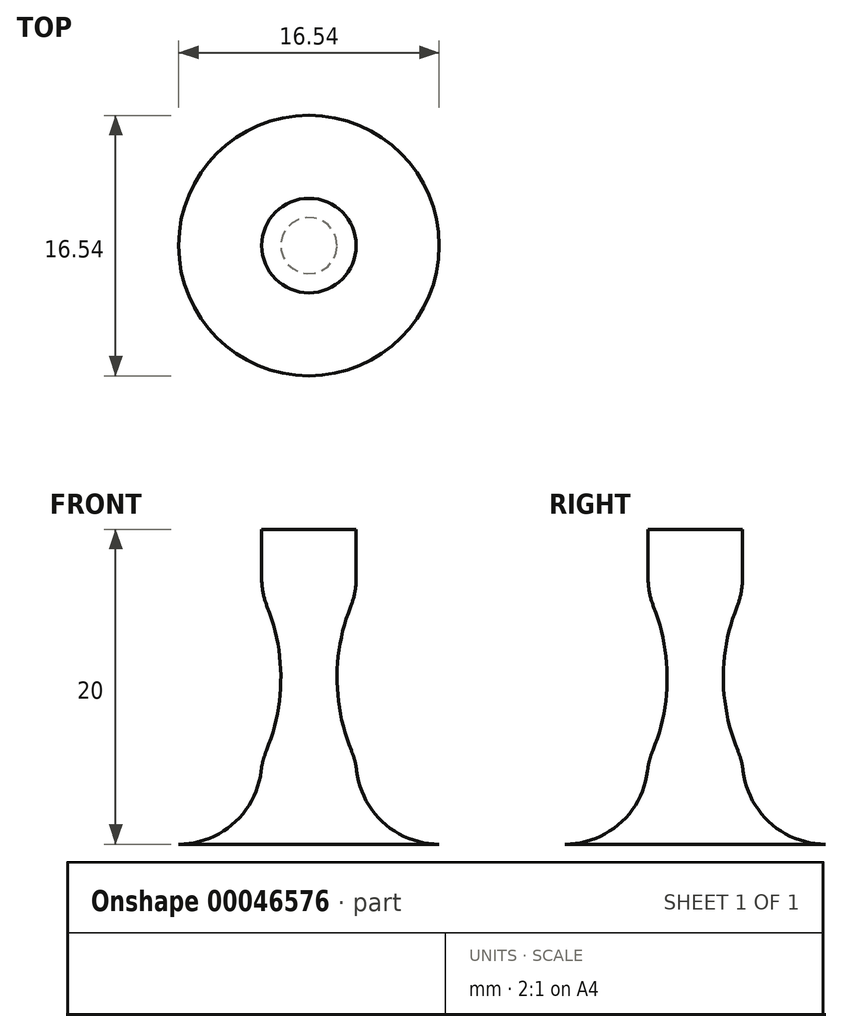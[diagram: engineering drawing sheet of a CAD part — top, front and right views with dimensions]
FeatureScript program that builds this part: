
annotation { "Feature Type Name" : "Feature", "Feature Type Description" : "" }
export const myFeature = defineFeature(function(context is Context, id is Id, definition is map)
    precondition{}
    {
        {
            var Q0;
            Q0=qCreatedBy(makeId("Front.planeOp"),FACE);
            var sketch = newSketch(context, id + "F0", { "sketchPlane" : qUnion([Q0])});
            skLineSegment(sketch, "E0", {"start": v(-3, 0) * mm, "end": v(0, 0) * mm});
            skLineSegment(sketch, "E1", {"start": v(0, 20) * mm, "end": v(0, 0) * mm});
            skLineSegment(sketch, "E2", {"start": v(0, 20) * mm, "end": v(-3, 20) * mm});
            skLineSegment(sketch, "E3", {"start": v(-3, 20) * mm, "end": v(-3, 15.88) * mm});
            skArc(sketch, "E4", {"start": v(-3, 5.27) * mm, "mid": v(-1.78, 10.58) * mm, "end": v(-3, 15.88) * mm});
            skLineSegment(sketch, "E5.trimOffspring", {"start": v(-3, 5.27) * mm, "end": v(-3, 0) * mm});
            skArc(sketch, "E6", {"start": v(-8.27, 0) * mm, "mid": v(-4.54, 1.54) * mm, "end": v(-3, 5.27) * mm});
            skLineSegment(sketch, "E7", {"start": v(-8.27, 0) * mm, "end": v(-3, 0) * mm});
            skSolve(sketch);
        }
        {
            var Q0;
            Q0 = qSketchRegion(id + "F0", true);
            var Q1;
            Q1=sQuery(id+"F0.wireOp",EDGE,"E1");
            revolve(context, id + "F1", {"entities" : qUnion([Q0]), "axis" : qUnion([Q1]), "revolveType" : RevolveType.FULL});
        }
        {
            var Q0;
            Q0=makeQuery(id+"F1.opRevolve","SWEPT_EDGE",EDGE,{"disambiguationData":[OSD([sQuery(id+"F0.wireOp",EDGE,"E3"),sQuery(id+"F0.wireOp",EDGE,"E4")])]});
            var Q1;
            Q1=makeQuery(id+"F1.opRevolve","SWEPT_EDGE",EDGE,{"disambiguationData":[OSD([sQuery(id+"F0.wireOp",EDGE,"E4"),sQuery(id+"F0.wireOp",EDGE,"E5.trimOffspring"),sQuery(id+"F0.wireOp",EDGE,"E6")])]});
            fillet(context, id + "F2", {"entities" : qUnion([Q0, Q1]), "radius" : 5 * mm, "tangentPropagation" : true, "allowEdgeOverflow" : false});
        }
    });
